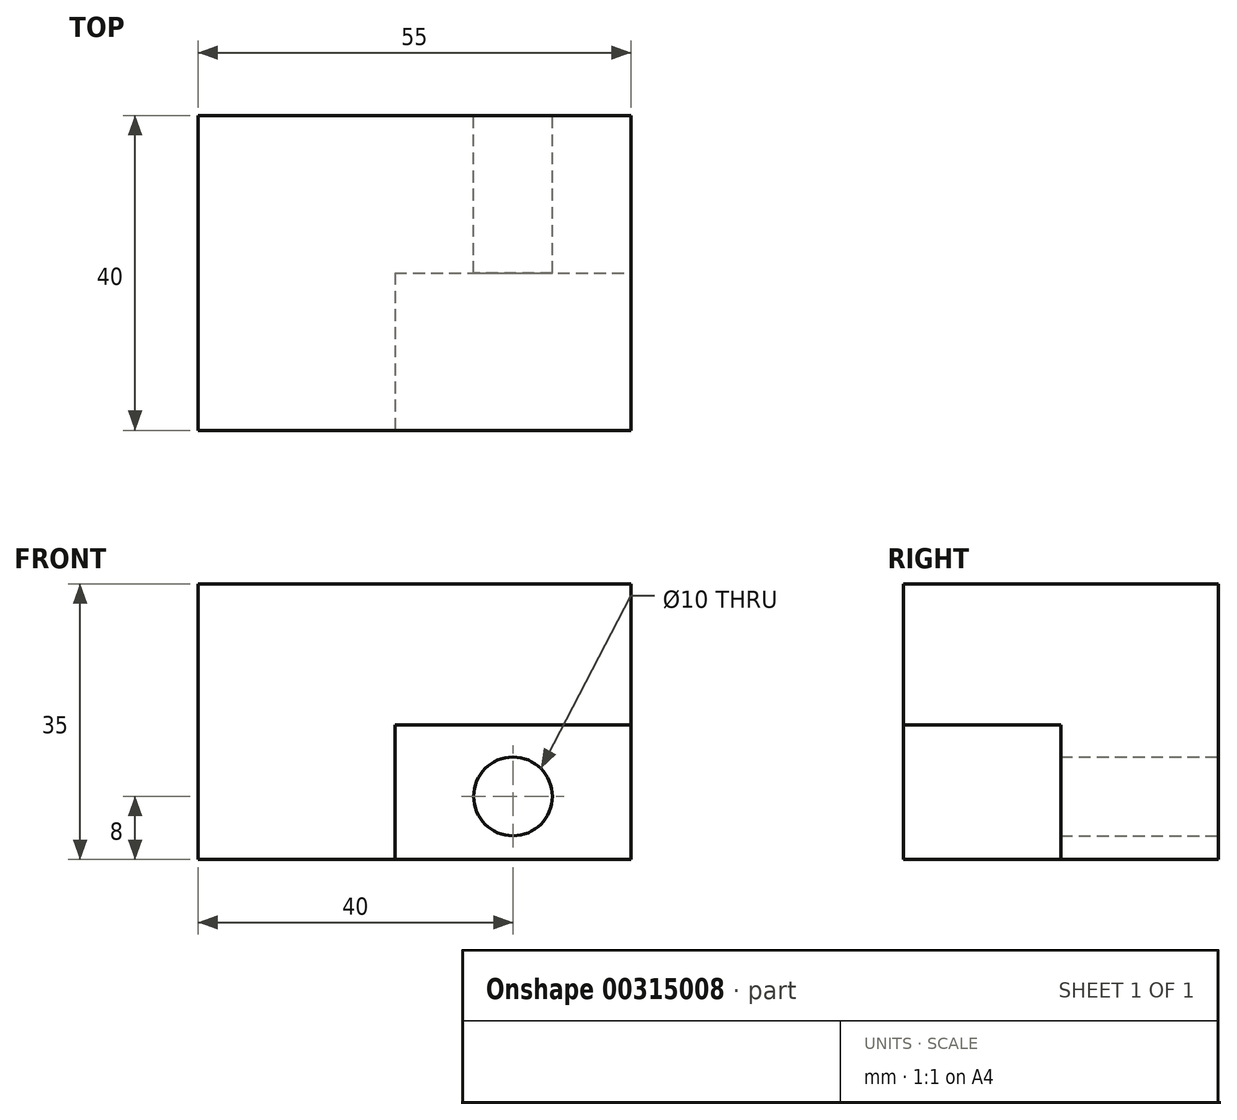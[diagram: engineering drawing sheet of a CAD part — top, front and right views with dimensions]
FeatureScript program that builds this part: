
annotation { "Feature Type Name" : "Feature", "Feature Type Description" : "" }
export const myFeature = defineFeature(function(context is Context, id is Id, definition is map)
    precondition{}
    {
        {
            var Q0;
            Q0=qCreatedBy(makeId("Front.planeOp"),FACE);
            var sketch = newSketch(context, id + "F0", { "sketchPlane" : qUnion([Q0])});
            skLineSegment(sketch, "E0.bottom", {"start": v(0, 0) * mm, "end": v(55, 0) * mm});
            skLineSegment(sketch, "E0.top", {"start": v(0, -35) * mm, "end": v(55, -35) * mm});
            skLineSegment(sketch, "E0.left", {"start": v(0, 0) * mm, "end": v(0, -35) * mm});
            skLineSegment(sketch, "E0.right", {"start": v(55, 0) * mm, "end": v(55, -35) * mm});
            skSolve(sketch);
        }
        {
            var Q0;
            Q0=makeQuery(id+"F0.imprint","IMPRINT",FACE,{"disambiguationData":[TD([[makeQuery(id+"F0.imprint","IMPRINT",EDGE,{"derivedFrom":sQuery(id+"F0.wireOp",EDGE,"E0.bottom")}),-1.0]])]});
            var Q1;
            Q1 = qSketchRegion(id + "F2", true);
            extrude(context, id + "F1", {"entities" : qUnion([Q0, Q1]), "depth" : 40 * mm});
        }
        {
            var Q0;
            Q0=makeQuery(id+"F1.opExtrude","CAP_FACE",FACE,{"disambiguationData":[OSD([sQuery(id+"F0.wireOp",EDGE,"E0.bottom"),sQuery(id+"F0.wireOp",EDGE,"E0.top"),sQuery(id+"F0.wireOp",EDGE,"E0.left"),sQuery(id+"F0.wireOp",EDGE,"E0.right")])],"isStart":false});
            var sketch = newSketch(context, id + "F2", { "sketchPlane" : qUnion([Q0])});
            skLineSegment(sketch, "E1.bottom", {"start": v(25, -17.93) * mm, "end": v(55, -17.93) * mm});
            skLineSegment(sketch, "E1.top", {"start": v(25, -35) * mm, "end": v(55, -35) * mm});
            skLineSegment(sketch, "E1.left", {"start": v(25, -17.93) * mm, "end": v(25, -35) * mm});
            skLineSegment(sketch, "E1.right", {"start": v(55, -17.93) * mm, "end": v(55, -35) * mm});
            skSolve(sketch);
        }
        {
            var Q0;
            Q0=makeQuery(id+"F2.imprint","IMPRINT",FACE,{"disambiguationData":[TD([[makeQuery(id+"F2.imprint","IMPRINT",EDGE,{"derivedFrom":sQuery(id+"F2.wireOp",EDGE,"E1.bottom")}),-1.0]])]});
            extrude(context, id + "F3", {"entities" : qUnion([Q0]), "operationType" : NewBodyOperationType.REMOVE, "oppositeDirection" : true, "depth" : 20 * mm});
        }
        {
            var Q0;
            Q0=qCreatedBy(makeId("Front.planeOp"),FACE);
            var sketch = newSketch(context, id + "F4", { "sketchPlane" : qUnion([Q0])});
            skCircle(sketch, "E2", {"center": v(40, -27) * mm, "radius": 5 * mm});
            skSolve(sketch);
        }
        {
            var Q0;
            Q0=makeQuery(id+"F4.imprint","IMPRINT",FACE,{"disambiguationData":[TD([[makeQuery(id+"F4.imprint","IMPRINT",EDGE,{"derivedFrom":sQuery(id+"F4.wireOp",EDGE,"E2")}),1.0]])]});
            extrude(context, id + "F5", {"entities" : qUnion([Q0]), "operationType" : NewBodyOperationType.REMOVE, "endBound" : BoundingType.THROUGH_ALL, "depth" : 25 * mm});
        }
    });
